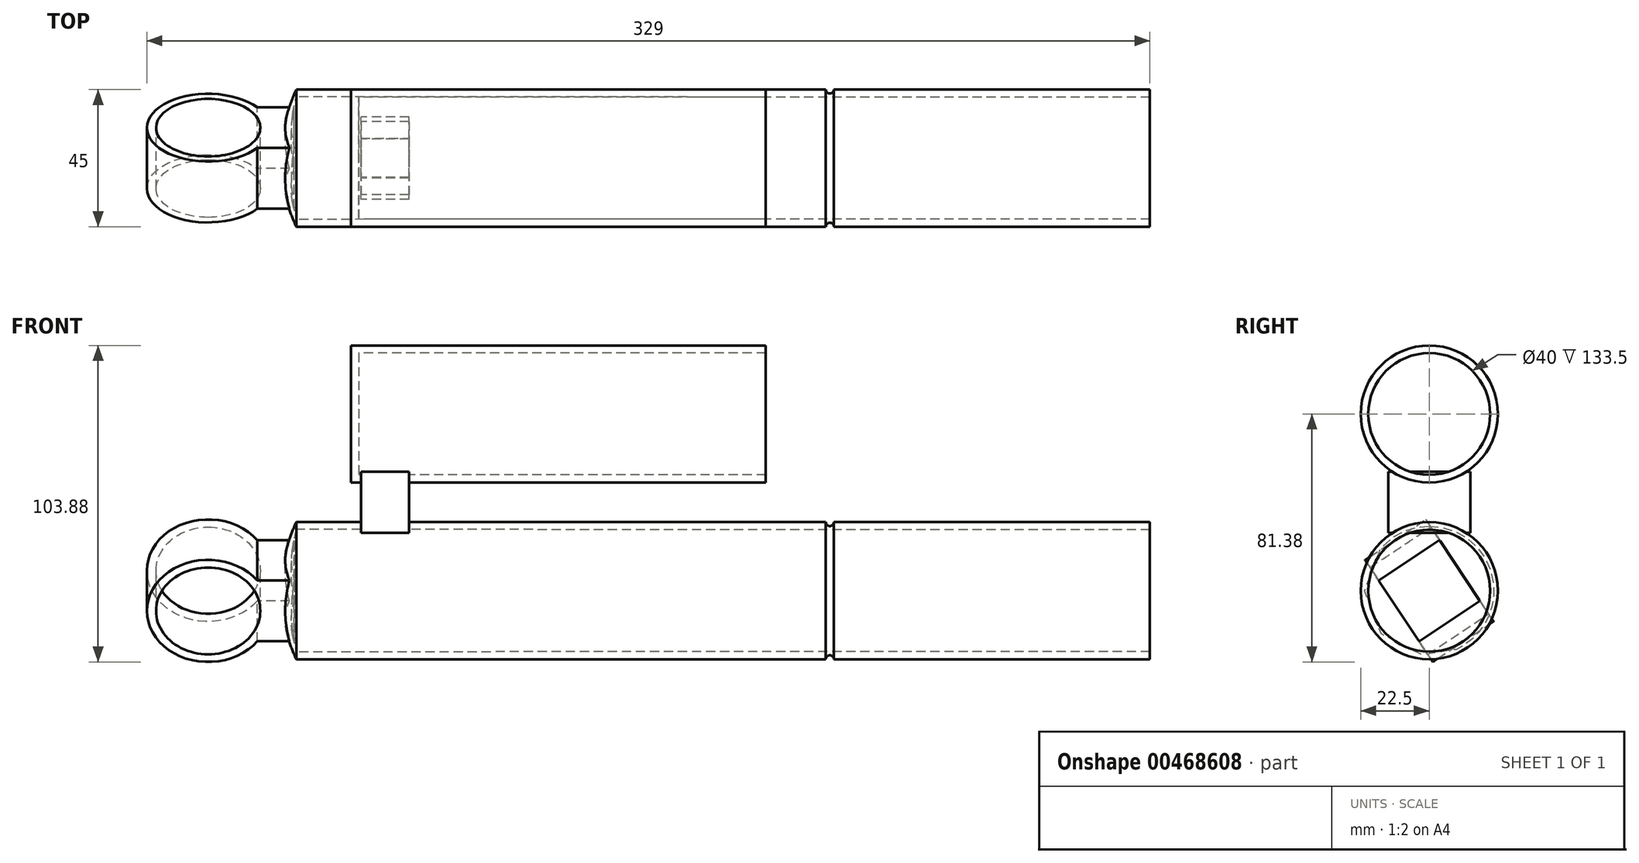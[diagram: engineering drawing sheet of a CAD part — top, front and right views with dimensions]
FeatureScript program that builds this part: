
annotation { "Feature Type Name" : "Feature", "Feature Type Description" : "" }
export const myFeature = defineFeature(function(context is Context, id is Id, definition is map)
    precondition{}
    {
        {
            var Q0;
            Q0=qCreatedBy(makeId("Front.planeOp"),FACE);
            var sketch = newSketch(context, id + "F0", { "sketchPlane" : qUnion([Q0])});
            skCircle(sketch, "E0", {"center": v(0, 0) * mm, "radius": 20.1 * mm, "construction": true});
            skPoint(sketch, "E1", {"position": v(308.9, 0) * mm});
            skLineSegment(sketch, "E2", {"start": v(308.9, 0) * mm, "end": v(308.9, 22.5) * mm});
            skLineSegment(sketch, "E3", {"start": v(308.9, 22.5) * mm, "end": v(205.2, 22.5) * mm});
            skLineSegment(sketch, "E4", {"start": v(28.9, 22.5) * mm, "end": v(28.9, 0) * mm});
            skLineSegment(sketch, "E5", {"start": v(28.9, 0) * mm, "end": v(308.9, 0) * mm, "construction": true});
            skPoint(sketch, "E6", {"position": v(308.9, 20) * mm});
            skLineSegment(sketch, "E7", {"start": v(308.9, 20) * mm, "end": v(28.9, 20.1) * mm});
            skPoint(sketch, "E7.endSnap0", {"position": v(28.9, 11.25) * mm});
            skPoint(sketch, "E8", {"position": v(23.9, 0) * mm});
            skPoint(sketch, "E9", {"position": v(28.9, -22.5) * mm});
            skPoint(sketch, "E10", {"position": v(28.9, -20) * mm});
            skArc(sketch, "E11", {"start": v(28.9, 22.5) * mm, "mid": v(25.17, 11.52) * mm, "end": v(23.9, 0) * mm});
            skArc(sketch, "E12", {"start": v(28.9, 20.1) * mm, "mid": v(27.02, 10.12) * mm, "end": v(26.4, 0) * mm});
            skLineSegment(sketch, "E13", {"start": v(23.9, 0) * mm, "end": v(26.4, 0) * mm});
            skArc(sketch, "E14", {"start": v(202.6, 22.5) * mm, "mid": v(203.9, 21.2) * mm, "end": v(205.2, 22.5) * mm});
            skLineSegment(sketch, "E15.trimOffspring", {"start": v(202.6, 22.5) * mm, "end": v(28.9, 22.5) * mm});
            skPoint(sketch, "E16", {"position": v(203.9, 21.2) * mm});
            skSolve(sketch);
        }
        {
            var Q0;
            Q0=qSketchRegion(id+"F0",true);
            var Q1;
            Q1=sQuery(id+"F0.wireOp",EDGE,"E5");
            revolve(context, id + "F1", {"entities" : qUnion([Q0]), "axis" : qUnion([Q1]), "revolveType" : RevolveType.FULL});
        }
        {
            var Q0;
            Q0=qCreatedBy(makeId("Front.planeOp"),FACE);
            var sketch = newSketch(context, id + "F2", { "sketchPlane" : qUnion([Q0])});
            skPoint(sketch, "E17", {"position": v(182.9, 58) * mm});
            skLineSegment(sketch, "E18", {"start": v(182.9, 58) * mm, "end": v(182.9, 80.5) * mm});
            skLineSegment(sketch, "E19", {"start": v(182.9, 80.5) * mm, "end": v(46.9, 80.5) * mm});
            skLineSegment(sketch, "E20", {"start": v(46.9, 80.5) * mm, "end": v(46.9, 58) * mm});
            skLineSegment(sketch, "E21", {"start": v(46.9, 58) * mm, "end": v(182.9, 58) * mm, "construction": true});
            skPoint(sketch, "E22", {"position": v(182.9, 78) * mm});
            skLineSegment(sketch, "E23", {"start": v(182.9, 78) * mm, "end": v(49.4, 78) * mm});
            skLineSegment(sketch, "E24", {"start": v(49.4, 78) * mm, "end": v(49.4, 58) * mm});
            skLineSegment(sketch, "E25", {"start": v(49.4, 58) * mm, "end": v(46.9, 58) * mm});
            skSolve(sketch);
        }
        {
            var Q0;
            Q0=qSketchRegion(id+"F2",true);
            var Q1;
            Q1=sQuery(id+"F2.wireOp",EDGE,"E21");
            revolve(context, id + "F3", {"entities" : qUnion([Q0]), "axis" : qUnion([Q1]), "revolveType" : RevolveType.FULL});
        }
        {
            var Q0;
            Q0=qCreatedBy(makeId("Front.planeOp"),FACE);
            var sketch = newSketch(context, id + "F4", { "sketchPlane" : qUnion([Q0])});
            skPoint(sketch, "E26", {"position": v(58, 29) * mm});
            skLineSegment(sketch, "E27.bottom", {"start": v(65.9, 39) * mm, "end": v(50.1, 39) * mm});
            skLineSegment(sketch, "E27.top", {"start": v(65.9, 19) * mm, "end": v(50.1, 19) * mm});
            skLineSegment(sketch, "E27.left", {"start": v(65.9, 39) * mm, "end": v(65.9, 19) * mm});
            skLineSegment(sketch, "E27.right", {"start": v(50.1, 39) * mm, "end": v(50.1, 19) * mm});
            skSolve(sketch);
        }
        {
            var Q0;
            Q0=qSketchRegion(id+"F4",true);
            extrude(context, id + "F5", {"entities" : qUnion([Q0]), "operationType" : NewBodyOperationType.ADD, "depth" : 27 * mm, "offsetDistance" : 25 * mm, "symmetric" : true});
        }
        {
            var Q0;
            Q0=qCreatedBy(makeId("Right.planeOp"),FACE);
            var sketch = newSketch(context, id + "F6", { "sketchPlane" : qUnion([Q0])});
            skLineSegment(sketch, "E28", {"start": v(-21.11, 10.12) * mm, "end": v(-1.11, 23.38) * mm});
            skLineSegment(sketch, "E29", {"start": v(-1.11, 23.38) * mm, "end": v(21.11, -10.12) * mm});
            skLineSegment(sketch, "E30", {"start": v(21.11, -10.12) * mm, "end": v(1.11, -23.38) * mm});
            skLineSegment(sketch, "E31", {"start": v(1.11, -23.38) * mm, "end": v(-21.11, 10.12) * mm});
            skPoint(sketch, "E32", {"position": v(10, 6.63) * mm});
            skPoint(sketch, "E33", {"position": v(-10, -6.63) * mm});
            skLineSegment(sketch, "E34", {"start": v(10, 6.63) * mm, "end": v(-10, -6.63) * mm, "construction": true});
            skPoint(sketch, "E35", {"position": v(11.11, -16.75) * mm});
            skPoint(sketch, "E36", {"position": v(-11.11, 16.75) * mm});
            skLineSegment(sketch, "E37", {"start": v(11.11, -16.75) * mm, "end": v(-11.11, 16.75) * mm, "construction": true});
            skPoint(sketch, "E38", {"position": v(0, 0) * mm});
            skLineSegment(sketch, "E39", {"start": v(0, 0) * mm, "end": v(-30, 0) * mm, "construction": true});
            skSolve(sketch);
        }
        {
            var Q0;
            Q0=qSketchRegion(id+"F6",true);
            extrude(context, id + "F7", {"entities" : qUnion([Q0]), "depth" : 40.2 * mm, "offsetDistance" : 25 * mm, "symmetric" : true});
        }
        {
            var Q0;
            Q0=makeQuery(id+"F7.opExtrude","SWEPT_FACE",FACE,{"disambiguationData":[OSD([sQuery(id+"F6.wireOp",EDGE,"E29")])]});
            var sketch = newSketch(context, id + "F8", { "sketchPlane" : qUnion([Q0])});
            skCircle(sketch, "E40", {"center": v(0, 0) * mm, "radius": 20.1 * mm});
            skCircle(sketch, "E41", {"center": v(0, 0) * mm, "radius": 17.1 * mm});
            skLineSegment(sketch, "E42.0", {"start": v(-20.1, -20.1) * mm, "end": v(20.1, -20.1) * mm});
            skLineSegment(sketch, "E43.0", {"start": v(-20.1, 20.1) * mm, "end": v(-20.1, -20.1) * mm});
            skLineSegment(sketch, "E44.0", {"start": v(20.1, 20.1) * mm, "end": v(20.1, -20.1) * mm});
            skLineSegment(sketch, "E45.0", {"start": v(-20.1, 20.1) * mm, "end": v(20.1, 20.1) * mm});
            skSolve(sketch);
        }
        {
            var Q0;
            {var subQ0=sQuery(id+"F8.wireOp",EDGE,"E42.0");var subQ1=sQuery(id+"F8.wireOp",EDGE,"E40");var subQ2=makeQuery(id+"F8.imprint","INTERSECT",VERTEX,{"derivedFrom":[subQ1,subQ0]});Q0=makeQuery(id+"F8.imprint","IMPRINT",FACE,{"disambiguationData":[TD([[makeQuery(id+"F8.imprint","IMPRINT",EDGE,{"disambiguationData":[TD([[subQ2,1.0]])],"derivedFrom":subQ1}),-1.0]])]});}
            var Q1;
            {var subQ0=sQuery(id+"F8.wireOp",EDGE,"E42.0");var subQ1=sQuery(id+"F8.wireOp",EDGE,"E40");var subQ2=makeQuery(id+"F8.imprint","INTERSECT",VERTEX,{"derivedFrom":[subQ1,subQ0]});Q1=makeQuery(id+"F8.imprint","IMPRINT",FACE,{"disambiguationData":[TD([[makeQuery(id+"F8.imprint","IMPRINT",EDGE,{"disambiguationData":[TD([[subQ2,-1.0]])],"derivedFrom":subQ1}),-1.0]])]});}
            var Q2;
            {var subQ0=sQuery(id+"F8.wireOp",EDGE,"E44.0");var subQ1=sQuery(id+"F8.wireOp",EDGE,"E40");var subQ2=makeQuery(id+"F8.imprint","INTERSECT",VERTEX,{"derivedFrom":[subQ1,subQ0]});Q2=makeQuery(id+"F8.imprint","IMPRINT",FACE,{"disambiguationData":[TD([[makeQuery(id+"F8.imprint","IMPRINT",EDGE,{"disambiguationData":[TD([[subQ2,-1.0]])],"derivedFrom":subQ1}),-1.0]])]});}
            var Q3;
            {var subQ0=sQuery(id+"F8.wireOp",EDGE,"E43.0");var subQ1=sQuery(id+"F8.wireOp",EDGE,"E40");var subQ2=makeQuery(id+"F8.imprint","INTERSECT",VERTEX,{"derivedFrom":[subQ1,subQ0]});Q3=makeQuery(id+"F8.imprint","IMPRINT",FACE,{"disambiguationData":[TD([[makeQuery(id+"F8.imprint","IMPRINT",EDGE,{"disambiguationData":[TD([[subQ2,1.0]])],"derivedFrom":subQ1}),-1.0]])]});}
            var Q4;
            Q4=makeQuery(id+"F8.imprint","IMPRINT",FACE,{"disambiguationData":[TD([[makeQuery(id+"F8.imprint","IMPRINT",EDGE,{"derivedFrom":sQuery(id+"F8.wireOp",EDGE,"E41")}),1.0]])]});
            extrude(context, id + "F9", {"entities" : qUnion([Q0, Q1, Q2, Q3, Q4]), "operationType" : NewBodyOperationType.REMOVE, "oppositeDirection" : true, "depth" : 25 * mm, "offsetDistance" : 25 * mm});
        }
        {
            var Q0;
            Q0=makeQuery(id+"F7.opExtrude","SWEPT_FACE",FACE,{"disambiguationData":[OSD([sQuery(id+"F6.wireOp",EDGE,"E29")])]});
            var sketch = newSketch(context, id + "F10", { "sketchPlane" : qUnion([Q0])});
            skCircle(sketch, "E46.0", {"center": v(0, 0) * mm, "radius": 20.1 * mm, "construction": true});
            skPoint(sketch, "E47", {"position": v(16.12, 12) * mm});
            skPoint(sketch, "E48", {"position": v(16.12, -12) * mm});
            skLineSegment(sketch, "E49", {"start": v(-16.12, 12) * mm, "end": v(-28.12, 12) * mm});
            skLineSegment(sketch, "E50", {"start": v(-28.12, 12) * mm, "end": v(-28.12, -12) * mm});
            skLineSegment(sketch, "E51", {"start": v(-28.12, -12) * mm, "end": v(-16.12, -12) * mm});
            skLineSegment(sketch, "E52", {"start": v(-16.12, -12) * mm, "end": v(-16.12, 12) * mm});
            skSolve(sketch);
        }
        {
            var Q0;
            {var subQ0=sQuery(id+"F10.wireOp",EDGE,"E49");Q0=makeQuery(id+"F10.imprint","IMPRINT",FACE,{"disambiguationData":[TD([[makeQuery(id+"F10.imprint","IMPRINT",EDGE,{"derivedFrom":subQ0}),1.0]])]});}
            extrude(context, id + "F11", {"entities" : qUnion([Q0]), "operationType" : NewBodyOperationType.ADD, "oppositeDirection" : true, "depth" : 24 * mm, "offsetDistance" : 25 * mm});
        }
    });
